# Revit family: SP4184W_EUR_Revit
name_source: partatom
category: Mechanical Equipment
revit_build: Autodesk Revit 2014 (Build: 20130215_1615(x64)
units: mm (PartAtom-declared; Revit-internal decimal feet)

## types (1)
- Standard
    Connector_10_Diameter = 0' - 0"
    Connector_11_Diameter = 0' - 0"
    Connector_12_Diameter = 0' - 0"
    Connector_13_Diameter = 0' - 0"
    Connector_1_Diameter = 0' - 0"
    Connector_2_Diameter = 0' - 0"
    Connector_3_Diameter = 0' - 0"
    Connector_8_Diameter = 0' - 0"
    Connector_9_Diameter = 0' - 0"
    Description = Electric Resistive Humidifier Weather proof
    Design Status = 1
    Manufacturer = Neptronic
    Model = SKE50-W, SKE60-W, SKE80-W
    Part Number = SP4184W_Revit
    URL = www.neptronic.com
    d101 = 0' - 1 7/16"
    d103 = 0' - 0 1/4"
    d105 = 0' - 0 1/4"
    d107 = 0' - 0 1/4"
    d109 = 0' - 0 1/4"
    d111 = 0' - 0 1/4"
    d113 = 0' - 0 1/4"
    d115 = 0' - 0 1/4"
    d117 = 0' - 0 1/4"
    d119 = 0' - 0 1/4"
    d121 = 0' - 0 1/4"
    d123 = 0' - 0 1/4"
    d125 = 0' - 0 1/4"
    d127 = 0' - 0 1/4"
    d129 = 0' - 0 9/32"
    d131 = 2' - 10 7/16"
    d133 = 1' - 1 13/16"
    d135 = 0' - 1"
    d95 = 0' - 1 7/16"
    d97 = 0' - 1 7/16"
    d99 = 0' - 1 7/16"

## geometry (parser evidence)
native form markers: Sweep x1
no freeform markers — native parametric forms only
